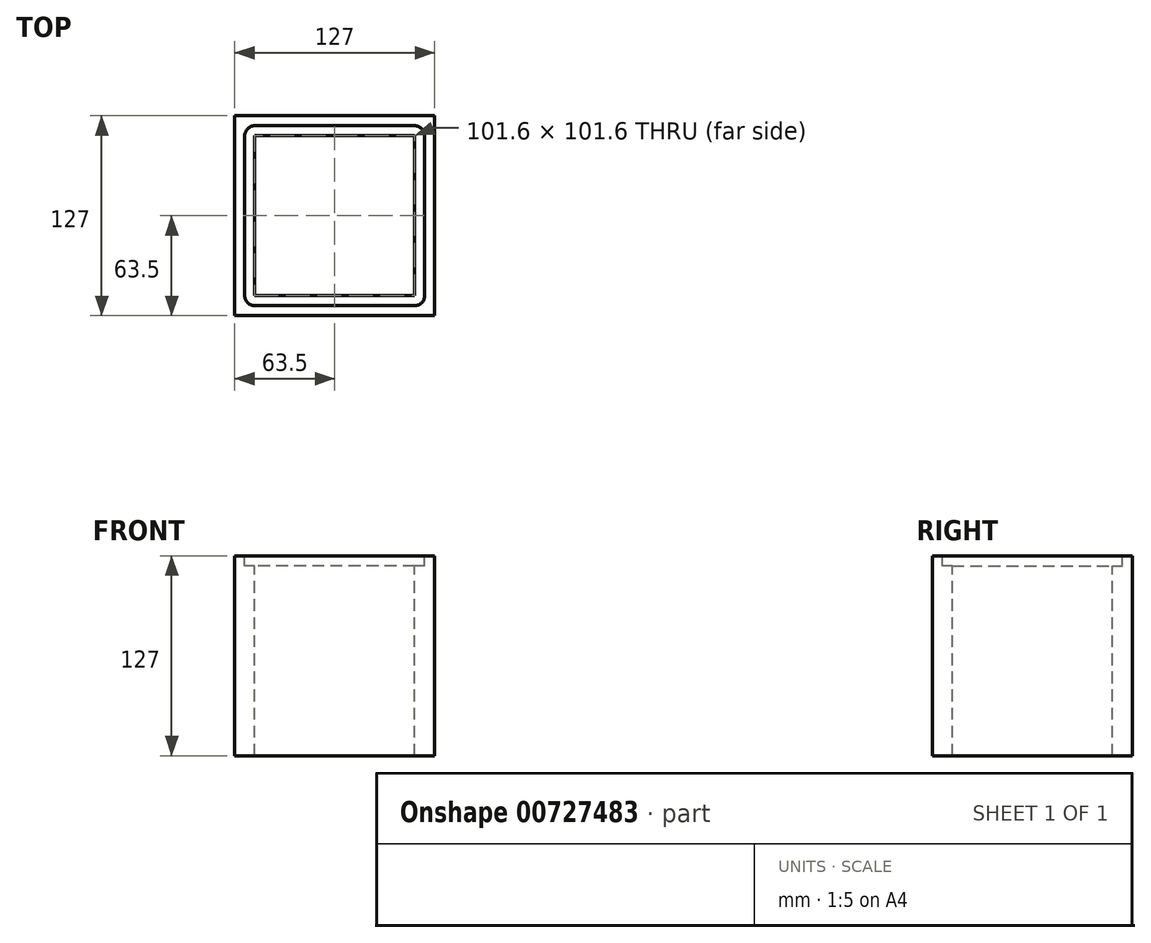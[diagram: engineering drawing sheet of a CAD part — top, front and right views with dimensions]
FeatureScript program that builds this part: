
annotation { "Feature Type Name" : "Feature", "Feature Type Description" : "" }
export const myFeature = defineFeature(function(context is Context, id is Id, definition is map)
    precondition{}
    {
        {
            var Q0;
            Q0=qCreatedBy(makeId("Top.planeOp"),FACE);
            var sketch = newSketch(context, id + "F0", { "sketchPlane" : qUnion([Q0])});
            skLineSegment(sketch, "E0.bottom", {"start": v(63.5, -63.5) * mm, "end": v(-63.5, -63.5) * mm});
            skLineSegment(sketch, "E0.top", {"start": v(63.5, 63.5) * mm, "end": v(-63.5, 63.5) * mm});
            skLineSegment(sketch, "E0.left", {"start": v(63.5, -63.5) * mm, "end": v(63.5, 63.5) * mm});
            skLineSegment(sketch, "E0.right", {"start": v(-63.5, -63.5) * mm, "end": v(-63.5, 63.5) * mm});
            skPoint(sketch, "E0.middle", {"position": v(0, 0) * mm});
            skSolve(sketch);
        }
        {
            var Q0;
            Q0=makeQuery(id+"F0.imprint","IMPRINT",FACE,{"disambiguationData":[TD([[makeQuery(id+"F0.imprint","IMPRINT",EDGE,{"derivedFrom":sQuery(id+"F0.wireOp",EDGE,"E0.bottom")}),-1.0]])]});
            extrude(context, id + "F1", {"entities" : qUnion([Q0]), "depth" : 127 * mm, "offsetDistance" : 25.4 * mm});
        }
        {
            var Q0;
            Q0=makeQuery(id+"F1.opExtrude","CAP_FACE",FACE,{"disambiguationData":[OSD([sQuery(id+"F0.wireOp",EDGE,"E0.bottom"),sQuery(id+"F0.wireOp",EDGE,"E0.top"),sQuery(id+"F0.wireOp",EDGE,"E0.left"),sQuery(id+"F0.wireOp",EDGE,"E0.right")])],"isStart":false});
            var sketch = newSketch(context, id + "F2", { "sketchPlane" : qUnion([Q0])});
            skLineSegment(sketch, "E1.bottom", {"start": v(50.8, -57.15) * mm, "end": v(-50.8, -57.15) * mm});
            skLineSegment(sketch, "E1.top", {"start": v(50.8, 57.15) * mm, "end": v(-50.8, 57.15) * mm});
            skLineSegment(sketch, "E1.left", {"start": v(57.15, -50.8) * mm, "end": v(57.15, 50.8) * mm});
            skLineSegment(sketch, "E1.right", {"start": v(-57.15, -50.8) * mm, "end": v(-57.15, 50.8) * mm});
            skPoint(sketch, "E1.middle", {"position": v(0, 0) * mm});
            skPoint(sketch, "E2.visualSharp", {"position": v(-57.15, 57.15) * mm});
            skArc(sketch, "E2.filletArc", {"start": v(-50.8, 57.15) * mm, "mid": v(-55.3, 55.3) * mm, "end": v(-57.15, 50.8) * mm});
            skPoint(sketch, "E3.visualSharp", {"position": v(57.15, 57.15) * mm});
            skArc(sketch, "E3.filletArc", {"start": v(57.15, 50.8) * mm, "mid": v(55.3, 55.3) * mm, "end": v(50.8, 57.15) * mm});
            skPoint(sketch, "E4.visualSharp", {"position": v(57.15, -57.15) * mm});
            skArc(sketch, "E4.filletArc", {"start": v(50.8, -57.15) * mm, "mid": v(55.3, -55.3) * mm, "end": v(57.15, -50.8) * mm});
            skPoint(sketch, "E5.visualSharp", {"position": v(-57.15, -57.15) * mm});
            skArc(sketch, "E5.filletArc", {"start": v(-57.15, -50.8) * mm, "mid": v(-55.3, -55.3) * mm, "end": v(-50.8, -57.15) * mm});
            skSolve(sketch);
        }
        {
            var Q0;
            Q0=makeQuery(id+"F2.imprint","IMPRINT",FACE,{"disambiguationData":[TD([[makeQuery(id+"F2.imprint","IMPRINT",EDGE,{"derivedFrom":sQuery(id+"F2.wireOp",EDGE,"E1.bottom")}),-1.0]])]});
            extrude(context, id + "F3", {"entities" : qUnion([Q0]), "operationType" : NewBodyOperationType.REMOVE, "oppositeDirection" : true, "depth" : 6.35 * mm, "offsetDistance" : 25.4 * mm});
        }
        {
            var Q0;
            Q0=makeQuery(id+"F3.boolean.opBoolean","COPY",FACE,{"derivedFrom":makeQuery(id+"F3.opExtrude","CAP_FACE",FACE,{"disambiguationData":[OSD([sQuery(id+"F2.wireOp",EDGE,"E1.bottom"),sQuery(id+"F2.wireOp",EDGE,"E1.top"),sQuery(id+"F2.wireOp",EDGE,"E1.left"),sQuery(id+"F2.wireOp",EDGE,"E1.right"),sQuery(id+"F2.wireOp",EDGE,"E2.filletArc"),sQuery(id+"F2.wireOp",EDGE,"E3.filletArc"),sQuery(id+"F2.wireOp",EDGE,"E4.filletArc"),sQuery(id+"F2.wireOp",EDGE,"E5.filletArc")])],"isStart":false})});
            var sketch = newSketch(context, id + "F4", { "sketchPlane" : qUnion([Q0])});
            skLineSegment(sketch, "E6.bottom", {"start": v(50.8, -50.8) * mm, "end": v(-50.8, -50.8) * mm});
            skLineSegment(sketch, "E6.top", {"start": v(50.8, 50.8) * mm, "end": v(-50.8, 50.8) * mm});
            skLineSegment(sketch, "E6.left", {"start": v(50.8, -50.8) * mm, "end": v(50.8, 50.8) * mm});
            skLineSegment(sketch, "E6.right", {"start": v(-50.8, -50.8) * mm, "end": v(-50.8, 50.8) * mm});
            skPoint(sketch, "E6.middle", {"position": v(0, 0) * mm});
            skSolve(sketch);
        }
        {
            var Q0;
            Q0=makeQuery(id+"F4.imprint","IMPRINT",FACE,{"disambiguationData":[TD([[makeQuery(id+"F4.imprint","IMPRINT",EDGE,{"derivedFrom":sQuery(id+"F4.wireOp",EDGE,"E6.bottom")}),-1.0]])]});
            extrude(context, id + "F5", {"entities" : qUnion([Q0]), "operationType" : NewBodyOperationType.REMOVE, "oppositeDirection" : true, "depth" : 127 * mm, "offsetDistance" : 25.4 * mm});
        }
    });
